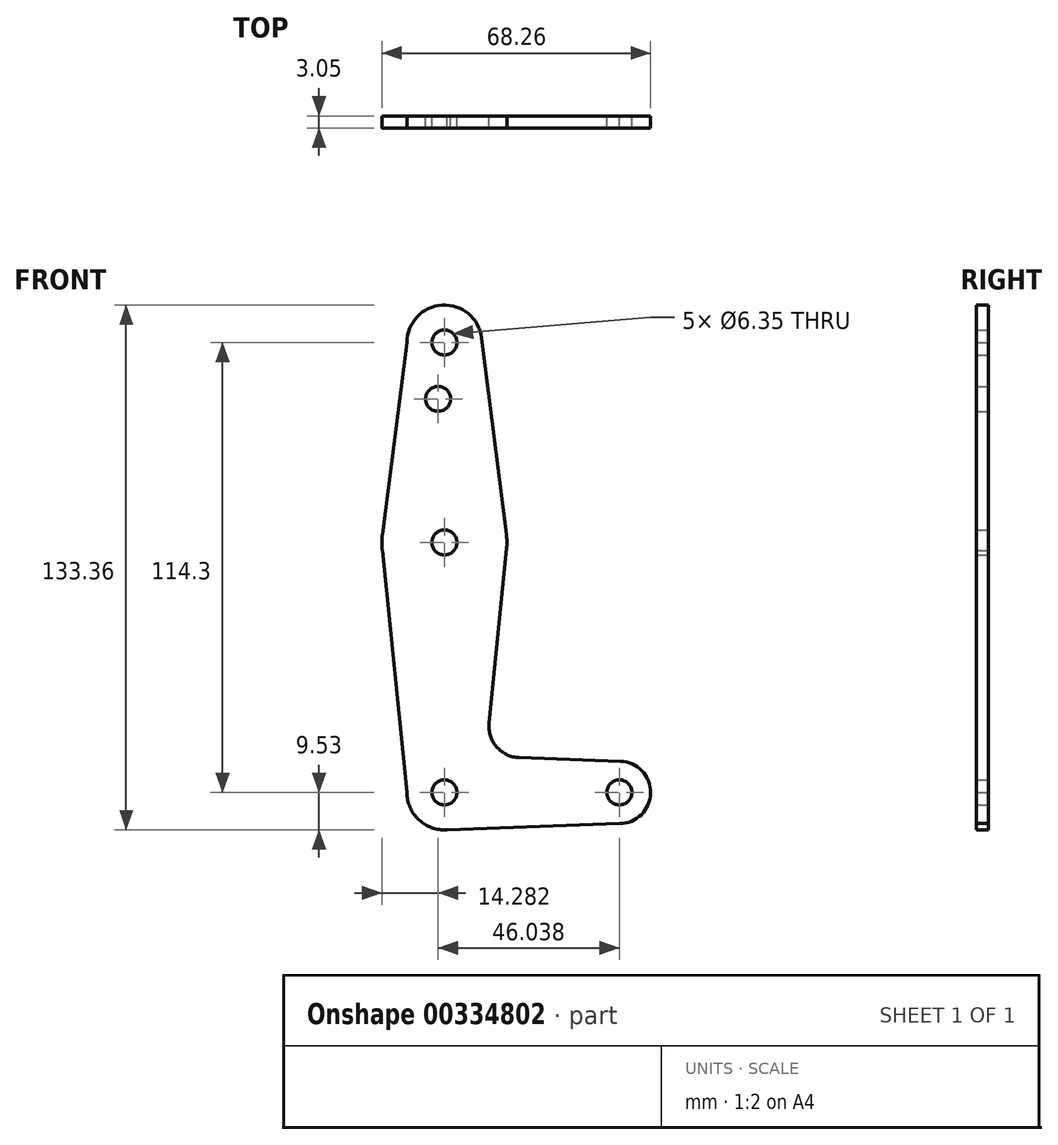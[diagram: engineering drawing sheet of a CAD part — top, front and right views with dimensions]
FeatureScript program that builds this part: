
annotation { "Feature Type Name" : "Feature", "Feature Type Description" : "" }
export const myFeature = defineFeature(function(context is Context, id is Id, definition is map)
    precondition{}
    {
        {
            var Q0;
            Q0=qCreatedBy(makeId("Front.planeOp"),FACE);
            var sketch = newSketch(context, id + "F0", { "sketchPlane" : qUnion([Q0])});
            skLineSegment(sketch, "E0", {"start": v(0, 0) * mm, "end": v(0, 114.3) * mm, "construction": true});
            skLineSegment(sketch, "E1", {"start": v(0, 0) * mm, "end": v(44.45, 0) * mm, "construction": true});
            skCircle(sketch, "E2", {"center": v(0, 114.3) * mm, "radius": 9.53 * mm});
            skCircle(sketch, "E3", {"center": v(0, 63.5) * mm, "radius": 15.88 * mm});
            skCircle(sketch, "E4", {"center": v(0, 0) * mm, "radius": 9.53 * mm});
            skCircle(sketch, "E5", {"center": v(44.45, 0) * mm, "radius": 7.94 * mm});
            skLineSegment(sketch, "E6", {"start": v(-9.53, 114.3) * mm, "end": v(-15.75, 65.5) * mm});
            skLineSegment(sketch, "E7", {"start": v(9.45, 115.5) * mm, "end": v(15.75, 65.48) * mm});
            skLineSegment(sketch, "E8", {"start": v(15.8, 61.91) * mm, "end": v(11.34, 17.59) * mm});
            skLineSegment(sketch, "E9", {"start": v(18.97, 8.85) * mm, "end": v(44.73, 7.93) * mm});
            skLineSegment(sketch, "E10", {"start": v(0, -9.52) * mm, "end": v(44.45, -7.94) * mm});
            skLineSegment(sketch, "E11", {"start": v(-9.52, 0) * mm, "end": v(-15.75, 61.5) * mm});
            skArc(sketch, "E12.filletArc", {"start": v(11.34, 17.59) * mm, "mid": v(13.26, 11.57) * mm, "end": v(18.97, 8.85) * mm});
            skCircle(sketch, "E13", {"center": v(0, 114.3) * mm, "radius": 3.18 * mm});
            skCircle(sketch, "E14", {"center": v(0, 63.5) * mm, "radius": 3.18 * mm});
            skCircle(sketch, "E15", {"center": v(0, 0) * mm, "radius": 3.18 * mm});
            skCircle(sketch, "E16", {"center": v(44.45, 0) * mm, "radius": 3.18 * mm});
            skCircle(sketch, "E17", {"center": v(-1.59, 100) * mm, "radius": 3.18 * mm});
            skSolve(sketch);
        }
        {
            var Q0;
            Q0 = qSketchRegion(id + "F0", true);
            extrude(context, id + "F1", {"entities" : qUnion([Q0]), "depth" : 3.05 * mm});
        }
    });
